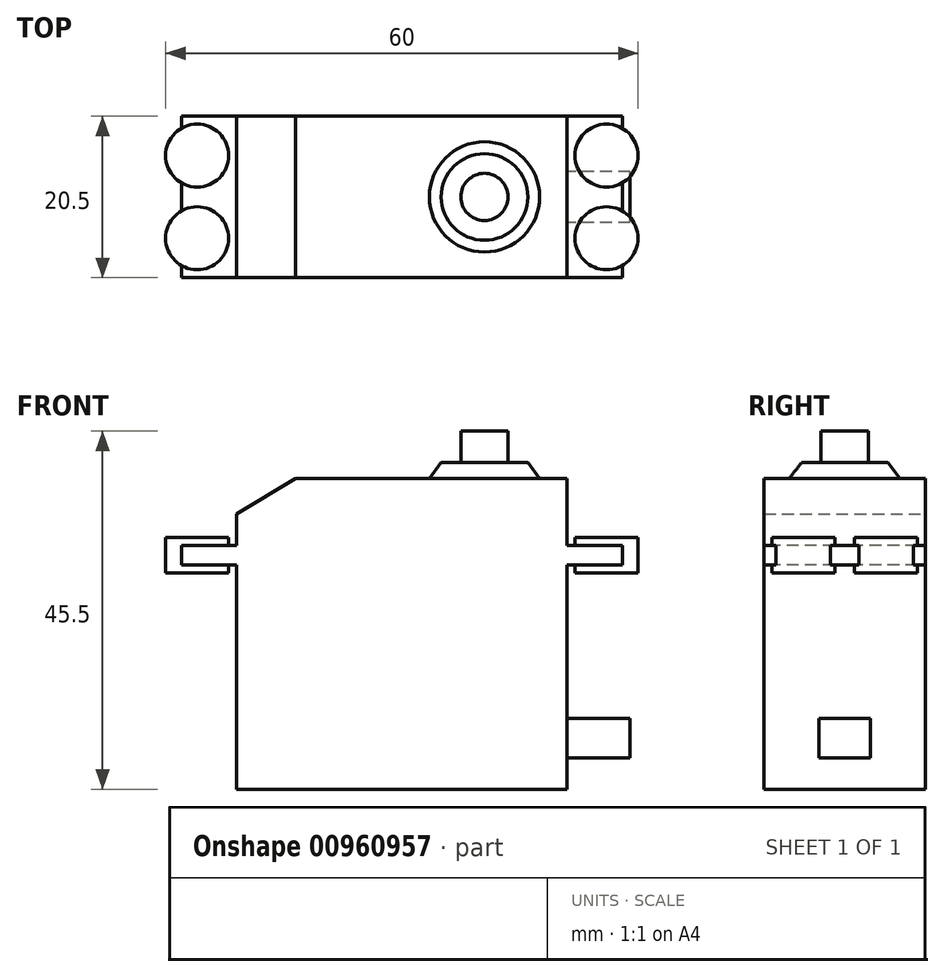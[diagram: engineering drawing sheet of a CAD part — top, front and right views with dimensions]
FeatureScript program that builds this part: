
annotation { "Feature Type Name" : "Feature", "Feature Type Description" : "" }
export const myFeature = defineFeature(function(context is Context, id is Id, definition is map)
    precondition{}
    {
        {
            var Q0;
            Q0=qCreatedBy(makeId("Top.planeOp"),FACE);
            var sketch = newSketch(context, id + "F0", { "sketchPlane" : qUnion([Q0])});
            skLineSegment(sketch, "E0.bottom", {"start": v(10.25, -31.5) * mm, "end": v(-10.25, -31.5) * mm});
            skLineSegment(sketch, "E0.top", {"start": v(10.25, 10.5) * mm, "end": v(-10.25, 10.5) * mm});
            skLineSegment(sketch, "E0.left", {"start": v(10.25, -31.5) * mm, "end": v(10.25, 10.5) * mm});
            skLineSegment(sketch, "E0.right", {"start": v(-10.25, -31.5) * mm, "end": v(-10.25, 10.5) * mm});
            skLineSegment(sketch, "E1", {"start": v(0, 0) * mm, "end": v(0, 10.5) * mm, "construction": true});
            skLineSegment(sketch, "E2", {"start": v(-10.25, 10.5) * mm, "end": v(-10.25, 17.5) * mm});
            skLineSegment(sketch, "E3", {"start": v(-10.25, 17.5) * mm, "end": v(-6.28, 17.5) * mm});
            skLineSegment(sketch, "E4", {"start": v(10.25, 17.5) * mm, "end": v(10.25, 10.5) * mm});
            skArc(sketch, "E5", {"start": v(-6.28, 17.5) * mm, "mid": v(-5.25, 13.25) * mm, "end": v(-4.22, 17.5) * mm});
            skLineSegment(sketch, "E6.trimOffspring", {"start": v(-4.22, 17.5) * mm, "end": v(4.22, 17.5) * mm});
            skArc(sketch, "E7.MirrorCS", {"start": v(6.28, 17.5) * mm, "mid": v(5.25, 13.25) * mm, "end": v(4.22, 17.5) * mm});
            skLineSegment(sketch, "E8.trimOffspring", {"start": v(6.28, 17.5) * mm, "end": v(10.25, 17.5) * mm});
            skLineSegment(sketch, "E9", {"start": v(-10.25, -10.5) * mm, "end": v(10.25, -10.5) * mm, "construction": true});
            skLineSegment(sketch, "E10.MirrorCS", {"start": v(-10.25, -31.5) * mm, "end": v(-10.25, -38.5) * mm});
            skLineSegment(sketch, "E11.MirrorCS", {"start": v(10.25, -38.5) * mm, "end": v(10.25, -31.5) * mm});
            skLineSegment(sketch, "E12.MirrorCS", {"start": v(6.28, -38.5) * mm, "end": v(10.25, -38.5) * mm});
            skLineSegment(sketch, "E13.MirrorCS", {"start": v(-4.22, -38.5) * mm, "end": v(4.22, -38.5) * mm});
            skArc(sketch, "E14.MirrorCS", {"start": v(6.28, -38.5) * mm, "mid": v(5.25, -34.25) * mm, "end": v(4.22, -38.5) * mm});
            skLineSegment(sketch, "E15.MirrorCS", {"start": v(-10.25, -38.5) * mm, "end": v(-6.28, -38.5) * mm});
            skArc(sketch, "E16.MirrorCS", {"start": v(-6.28, -38.5) * mm, "mid": v(-5.25, -34.25) * mm, "end": v(-4.22, -38.5) * mm});
            skSolve(sketch);
        }
        {
            var Q0;
            Q0=makeQuery(id+"F0.imprint","IMPRINT",FACE,{"disambiguationData":[TD([[makeQuery(id+"F0.imprint","IMPRINT",EDGE,{"derivedFrom":sQuery(id+"F0.wireOp",EDGE,"V9pWSfIz-jkMJ-fkbC-dAUF-8p46Ey4bh1Nl")}),1.0]])]});
            var Q1;
            Q1=makeQuery(id+"F0.imprint","IMPRINT",FACE,{"disambiguationData":[TD([[makeQuery(id+"F0.imprint","IMPRINT",EDGE,{"derivedFrom":sQuery(id+"F0.wireOp",EDGE,"hd3io4hl-mZZM-ydez-IL9K-n6QVvt6htlZV")}),-1.0]])]});
            var Q2;
            Q2=makeQuery(id+"F0.imprint","IMPRINT",FACE,{"disambiguationData":[TD([[makeQuery(id+"F0.imprint","IMPRINT",EDGE,{"derivedFrom":sQuery(id+"F0.wireOp",EDGE,"hd3io4hl-mZZM-ydez-IL9K-n6QVvt6htlZV")}),1.0]])]});
            var Q3;
            Q3=makeQuery(id+"F0.imprint","IMPRINT",FACE,{"disambiguationData":[TD([[makeQuery(id+"F0.imprint","IMPRINT",EDGE,{"derivedFrom":sQuery(id+"F0.wireOp",EDGE,"E0.bottom")}),-1.0]])]});
            extrude(context, id + "F1", {"entities" : qUnion([Q0, Q1, Q2, Q3]), "depth" : 39.5 * mm, "offsetDistance" : 25 * mm});
        }
        {
            var Q0;
            Q0=makeQuery(id+"F0.imprint","IMPRINT",FACE,{"disambiguationData":[TD([[makeQuery(id+"F0.imprint","IMPRINT",EDGE,{"derivedFrom":sQuery(id+"F0.wireOp",EDGE,"E0.top")}),-1.0]])]});
            var Q1;
            Q1=makeQuery(id+"F0.imprint","IMPRINT",FACE,{"disambiguationData":[TD([[makeQuery(id+"F0.imprint","IMPRINT",EDGE,{"derivedFrom":sQuery(id+"F0.wireOp",EDGE,"E0.bottom")}),1.0]])]});
            extrude(context, id + "F2", {"entities" : qUnion([Q0, Q1]), "operationType" : NewBodyOperationType.ADD, "depth" : 11 * mm, "offsetDistance" : 25 * mm, "hasSecondDirection" : true, "secondDirectionOppositeDirection" : false, "secondDirectionDepth" : (11 - 2.5) * mm});
        }
        {
            var Q0;
            Q0=qCreatedBy(makeId("Right.planeOp"),FACE);
            var sketch = newSketch(context, id + "F3", { "sketchPlane" : qUnion([Q0])});
            skLineSegment(sketch, "E17", {"start": v(7, 0) * mm, "end": v(5.5, -2) * mm});
            skLineSegment(sketch, "E18", {"start": v(5.5, -2) * mm, "end": v(3, -2) * mm});
            skLineSegment(sketch, "E19", {"start": v(3, -2) * mm, "end": v(3, -6) * mm});
            skLineSegment(sketch, "E20", {"start": v(3, -6) * mm, "end": v(0, -6) * mm});
            skLineSegment(sketch, "E21", {"start": v(0, -6) * mm, "end": v(0, 0) * mm});
            skLineSegment(sketch, "E22", {"start": v(0, 0) * mm, "end": v(7, 0) * mm});
            skPoint(sketch, "E23", {"position": v(0, -6) * mm});
            skSolve(sketch);
        }
        {
            var Q0;
            Q0 = qSketchRegion(id + "F3", true);
            var Q1;
            Q1=sQuery(id+"F3.wireOp",EDGE,"E21");
            revolve(context, id + "F4", {"operationType" : NewBodyOperationType.ADD, "surfaceOperationType" : NewSurfaceOperationType.NEW, "entities" : qUnion([Q0]), "axis" : qUnion([Q1]), "revolveType" : RevolveType.FULL});
        }
        {
            var Q0;
            {var subQ2=sQuery(id+"F0.wireOp",EDGE,"E0.top");var subQ3=sQuery(id+"F0.wireOp",EDGE,"E0.right");var subQ4=sQuery(id+"F0.wireOp",EDGE,"E0.left");Q0=makeQuery(id+"F2.boolean.opBoolean","SPLIT",FACE,{"disambiguationData":[TD([makeQuery(id+"F1.opExtrude","CAP_FACE",FACE,{"disambiguationData":[OSD([sQuery(id+"F0.wireOp",EDGE,"E0.bottom"),subQ2,subQ4,subQ3])],"isStart":false})])],"derivedFrom":makeQuery(id+"F1.opExtrude","SWEPT_FACE",FACE,{"disambiguationData":[OSD([subQ2])]})});}
            var sketch = newSketch(context, id + "F5", { "sketchPlane" : qUnion([Q0])});
            skLineSegment(sketch, "E24", {"start": v(0, 39.5) * mm, "end": v(0, 35.5) * mm, "construction": true});
            skLineSegment(sketch, "E25.bottom", {"start": v(3.25, 35.5) * mm, "end": v(-3.25, 35.5) * mm});
            skLineSegment(sketch, "E25.top", {"start": v(3.25, 30.5) * mm, "end": v(-3.25, 30.5) * mm});
            skLineSegment(sketch, "E25.left", {"start": v(3.25, 35.5) * mm, "end": v(3.25, 30.5) * mm});
            skLineSegment(sketch, "E25.right", {"start": v(-3.25, 35.5) * mm, "end": v(-3.25, 30.5) * mm});
            skPoint(sketch, "E25.middle", {"position": v(0, 33) * mm});
            skSolve(sketch);
        }
        {
            var Q0;
            Q0=makeQuery(id+"F5.imprint","IMPRINT",FACE,{"disambiguationData":[TD([[makeQuery(id+"F5.imprint","IMPRINT",EDGE,{"derivedFrom":sQuery(id+"F5.wireOp",EDGE,"E25.bottom")}),1.0]])]});
            extrude(context, id + "F6", {"entities" : qUnion([Q0]), "operationType" : NewBodyOperationType.ADD, "depth" : 8 * mm, "offsetDistance" : 25 * mm});
        }
        {
            var Q0;
            Q0=makeQuery(id+"F1.opExtrude","CAP_EDGE",EDGE,{"disambiguationData":[OSD([sQuery(id+"F0.wireOp",EDGE,"E0.bottom")])],"isStart":true});
            chamfer(context, id + "F7", {"entities" : qUnion([Q0]), "chamferType" : ChamferType.TWO_OFFSETS, "width1" : 7.5 * mm, "oppositeDirection" : false, "width2" : 4.5 * mm});
        }
        {
            var Q0;
            Q0=makeQuery(id+"F2.opExtrude","CAP_FACE",FACE,{"disambiguationData":[OSD([sQuery(id+"F0.wireOp",EDGE,"E0.top"),sQuery(id+"F0.wireOp",EDGE,"E2"),sQuery(id+"F0.wireOp",EDGE,"E3"),sQuery(id+"F0.wireOp",EDGE,"E4"),sQuery(id+"F0.wireOp",EDGE,"E5"),sQuery(id+"F0.wireOp",EDGE,"E6.trimOffspring"),sQuery(id+"F0.wireOp",EDGE,"E7.MirrorCS"),sQuery(id+"F0.wireOp",EDGE,"E8.trimOffspring")])],"isStart":true});
            var sketch = newSketch(context, id + "F8", { "sketchPlane" : qUnion([Q0])});
            skArc(sketch, "E26.0", {"start": v(-6.28, -17.5) * mm, "mid": v(-5.25, -13.25) * mm, "end": v(-4.22, -17.5) * mm});
            skArc(sketch, "E27.0", {"start": v(6.28, -17.5) * mm, "mid": v(5.25, -13.25) * mm, "end": v(4.22, -17.5) * mm});
            skCircle(sketch, "E28", {"center": v(-5.25, -15.5) * mm, "radius": 4 * mm});
            skCircle(sketch, "E29", {"center": v(5.25, -15.5) * mm, "radius": 4 * mm});
            skArc(sketch, "E30.0", {"start": v(6.28, 38.5) * mm, "mid": v(5.25, 34.25) * mm, "end": v(4.22, 38.5) * mm});
            skArc(sketch, "E31.0", {"start": v(-6.28, 38.5) * mm, "mid": v(-5.25, 34.25) * mm, "end": v(-4.22, 38.5) * mm});
            skCircle(sketch, "E32", {"center": v(-5.25, 36.5) * mm, "radius": 4 * mm});
            skCircle(sketch, "E33", {"center": v(5.25, 36.5) * mm, "radius": 4 * mm});
            skSolve(sketch);
        }
        {
            var Q0;
            Q0=makeQuery(id+"F8.imprint","IMPRINT",FACE,{"disambiguationData":[TD([[makeQuery(id+"F8.imprint","IMPRINT",EDGE,{"derivedFrom":sQuery(id+"F8.wireOp",EDGE,"E32")}),1.0]])]});
            var Q1;
            Q1=makeQuery(id+"F8.imprint","IMPRINT",FACE,{"disambiguationData":[TD([[makeQuery(id+"F8.imprint","IMPRINT",EDGE,{"derivedFrom":sQuery(id+"F8.wireOp",EDGE,"E33")}),1.0]])]});
            var Q2;
            {var subQ0=sQuery(id+"F8.wireOp",EDGE,"E27.0");Q2=makeQuery(id+"F8.imprint","IMPRINT",FACE,{"disambiguationData":[TD([[makeQuery(id+"F8.imprint","IMPRINT",EDGE,{"derivedFrom":subQ0}),1.0]])]});}
            var Q3;
            {var subQ0=sQuery(id+"F8.wireOp",EDGE,"E26.0");Q3=makeQuery(id+"F8.imprint","IMPRINT",FACE,{"disambiguationData":[TD([[makeQuery(id+"F8.imprint","IMPRINT",EDGE,{"derivedFrom":subQ0}),1.0]])]});}
            var Q4;
            {var subQ0=sQuery(id+"F8.wireOp",EDGE,"E26.0");Q4=makeQuery(id+"F8.imprint","IMPRINT",FACE,{"disambiguationData":[TD([[makeQuery(id+"F8.imprint","IMPRINT",EDGE,{"derivedFrom":subQ0}),-1.0]])]});}
            var Q5;
            {var subQ0=sQuery(id+"F8.wireOp",EDGE,"E27.0");Q5=makeQuery(id+"F8.imprint","IMPRINT",FACE,{"disambiguationData":[TD([[makeQuery(id+"F8.imprint","IMPRINT",EDGE,{"derivedFrom":subQ0}),-1.0]])]});}
            var Q6;
            Q6=makeQuery(id+"F2.opExtrude","CAP_FACE",FACE,{"disambiguationData":[OSD([sQuery(id+"F0.wireOp",EDGE,"E0.top"),sQuery(id+"F0.wireOp",EDGE,"E2"),sQuery(id+"F0.wireOp",EDGE,"E3"),sQuery(id+"F0.wireOp",EDGE,"E4"),sQuery(id+"F0.wireOp",EDGE,"E5"),sQuery(id+"F0.wireOp",EDGE,"E6.trimOffspring"),sQuery(id+"F0.wireOp",EDGE,"E7.MirrorCS"),sQuery(id+"F0.wireOp",EDGE,"E8.trimOffspring")])],"isStart":false});
            extrude(context, id + "F9", {"entities" : qUnion([Q0, Q1, Q2, Q3, Q4, Q5]), "operationType" : NewBodyOperationType.ADD, "depth" : 1 * mm, "offsetDistance" : 25 * mm, "hasSecondDirection" : true, "secondDirectionBound" : SecondDirectionBoundingType.UP_TO_SURFACE, "secondDirectionOppositeDirection" : true, "secondDirectionDepth" : 1 * mm, "secondDirectionBoundEntityFace" : qUnion([Q6]), "hasSecondDirectionOffset" : true, "secondDirectionOffsetDistance" : 1 * mm, "secondDirectionOffsetOppositeDirection" : true});
        }
        {
            var Q0;
            Q0=makeQuery(id+"F1.opExtrude","SWEPT_BODY",BODY,{"disambiguationData":[OSD([sQuery(id+"F0.wireOp",EDGE,"E0.bottom"),sQuery(id+"F0.wireOp",EDGE,"E0.top"),sQuery(id+"F0.wireOp",EDGE,"E0.left"),sQuery(id+"F0.wireOp",EDGE,"E0.right")])]});
            var Q1;
            Q1=sQuery(id+"F0.wireOp",EDGE,"E1");
            transform(context, id + "F10", {"entities" : qUnion([Q0]), "transformType" : TransformType.ROTATION, "transformAxis" : qUnion([Q1]), "angle" : 180 * degree, "makeCopy" : false});
        }
        {
            var Q0;
            Q0=makeQuery(id+"F1.opExtrude","SWEPT_BODY",BODY,{"disambiguationData":[OSD([sQuery(id+"F0.wireOp",EDGE,"E0.bottom"),sQuery(id+"F0.wireOp",EDGE,"E0.top"),sQuery(id+"F0.wireOp",EDGE,"E0.left"),sQuery(id+"F0.wireOp",EDGE,"E0.right")])]});
            var Q1;
            Q1=qCreatedBy(makeId("Origin.pointOp"),VERTEX);
            var Q2;
            Q2=sQuery(id+"F3.wireOp",VERTEX,"E20.end");
            transform(context, id + "F11", {"entities" : qUnion([Q0]), "transformType" : TransformType.TRANSLATION_ENTITY, "oppositeDirectionEntity" : false, "transformLine" : qUnion([Q1, Q2]), "makeCopy" : false});
        }
        {
            var Q0;
            Q0=makeQuery(id+"F1.opExtrude","SWEPT_BODY",BODY,{"disambiguationData":[OSD([sQuery(id+"F0.wireOp",EDGE,"E0.bottom"),sQuery(id+"F0.wireOp",EDGE,"E0.top"),sQuery(id+"F0.wireOp",EDGE,"E0.left"),sQuery(id+"F0.wireOp",EDGE,"E0.right")])]});
            var Q1;
            Q1=sQuery(id+"F3.wireOp",EDGE,"E21");
            transform(context, id + "F12", {"entities" : qUnion([Q0]), "transformType" : TransformType.ROTATION, "transformAxis" : qUnion([Q1]), "angle" : 90 * degree, "oppositeDirection" : true, "makeCopy" : false});
        }
    });
